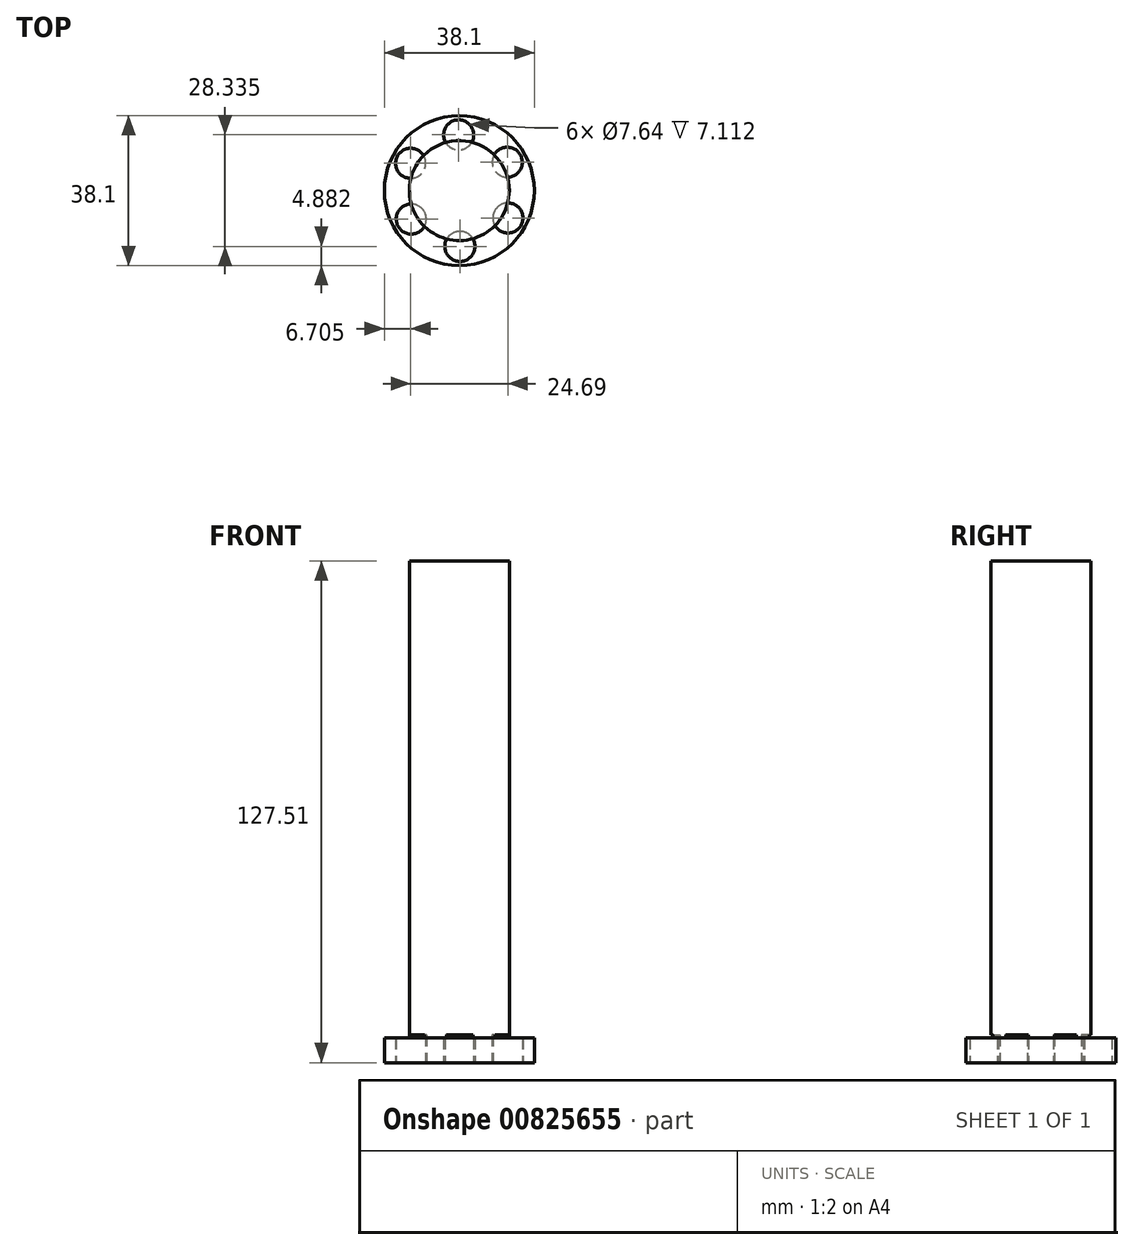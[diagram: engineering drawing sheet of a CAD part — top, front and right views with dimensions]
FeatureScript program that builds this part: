
annotation { "Feature Type Name" : "Feature", "Feature Type Description" : "" }
export const myFeature = defineFeature(function(context is Context, id is Id, definition is map)
    precondition{}
    {
        {
            var Q0;
            Q0=qCreatedBy(makeId("Top.planeOp"),FACE);
            var sketch = newSketch(context, id + "F0", { "sketchPlane" : qUnion([Q0])});
            skCircle(sketch, "E0", {"center": v(0, 0) * mm, "radius": 12.7 * mm});
            skSolve(sketch);
        }
        {
            var Q0;
            Q0 = qSketchRegion(id + "F0", true);
            extrude(context, id + "F1", {"entities" : qUnion([Q0]), "depth" : 127.5 * mm, "offsetDistance" : 25.4 * mm});
        }
        {
            var Q0;
            Q0=qCreatedBy(makeId("Top.planeOp"),FACE);
            var sketch = newSketch(context, id + "F2", { "sketchPlane" : qUnion([Q0])});
            skCircle(sketch, "E1", {"center": v(0, 0) * mm, "radius": 19.05 * mm});
            skSolve(sketch);
        }
        {
            var Q0;
            Q0 = qSketchRegion(id + "F2", true);
            extrude(context, id + "F3", {"entities" : qUnion([Q0]), "operationType" : NewBodyOperationType.ADD, "depth" : 6.35 * mm, "offsetDistance" : 25.4 * mm});
        }
        {
            var Q0;
            Q0=qCreatedBy(makeId("Top.planeOp"),FACE);
            var sketch = newSketch(context, id + "F4", { "sketchPlane" : qUnion([Q0])});
            skCircle(sketch, "E2", {"center": v(12.2, 7.21) * mm, "radius": 3.82 * mm});
            skCircle(sketch, "E3.1.0", {"center": v(-0.15, 14.17) * mm, "radius": 3.82 * mm});
            skCircle(sketch, "E3.2.0", {"center": v(-12.34, 6.95) * mm, "radius": 3.82 * mm});
            skCircle(sketch, "E3.3.0", {"center": v(-12.2, -7.21) * mm, "radius": 3.82 * mm});
            skCircle(sketch, "E3.4.0", {"center": v(0.15, -14.17) * mm, "radius": 3.82 * mm});
            skCircle(sketch, "E3.5.0", {"center": v(12.34, -6.95) * mm, "radius": 3.82 * mm});
            skPoint(sketch, "E3.center", {"position": v(0, 0) * mm});
            skSolve(sketch);
        }
        {
            var Q0;
            Q0 = qSketchRegion(id + "F4", true);
            extrude(context, id + "F5", {"entities" : qUnion([Q0]), "operationType" : NewBodyOperationType.REMOVE, "depth" : 7.11 * mm, "offsetDistance" : 25.4 * mm});
        }
    });
